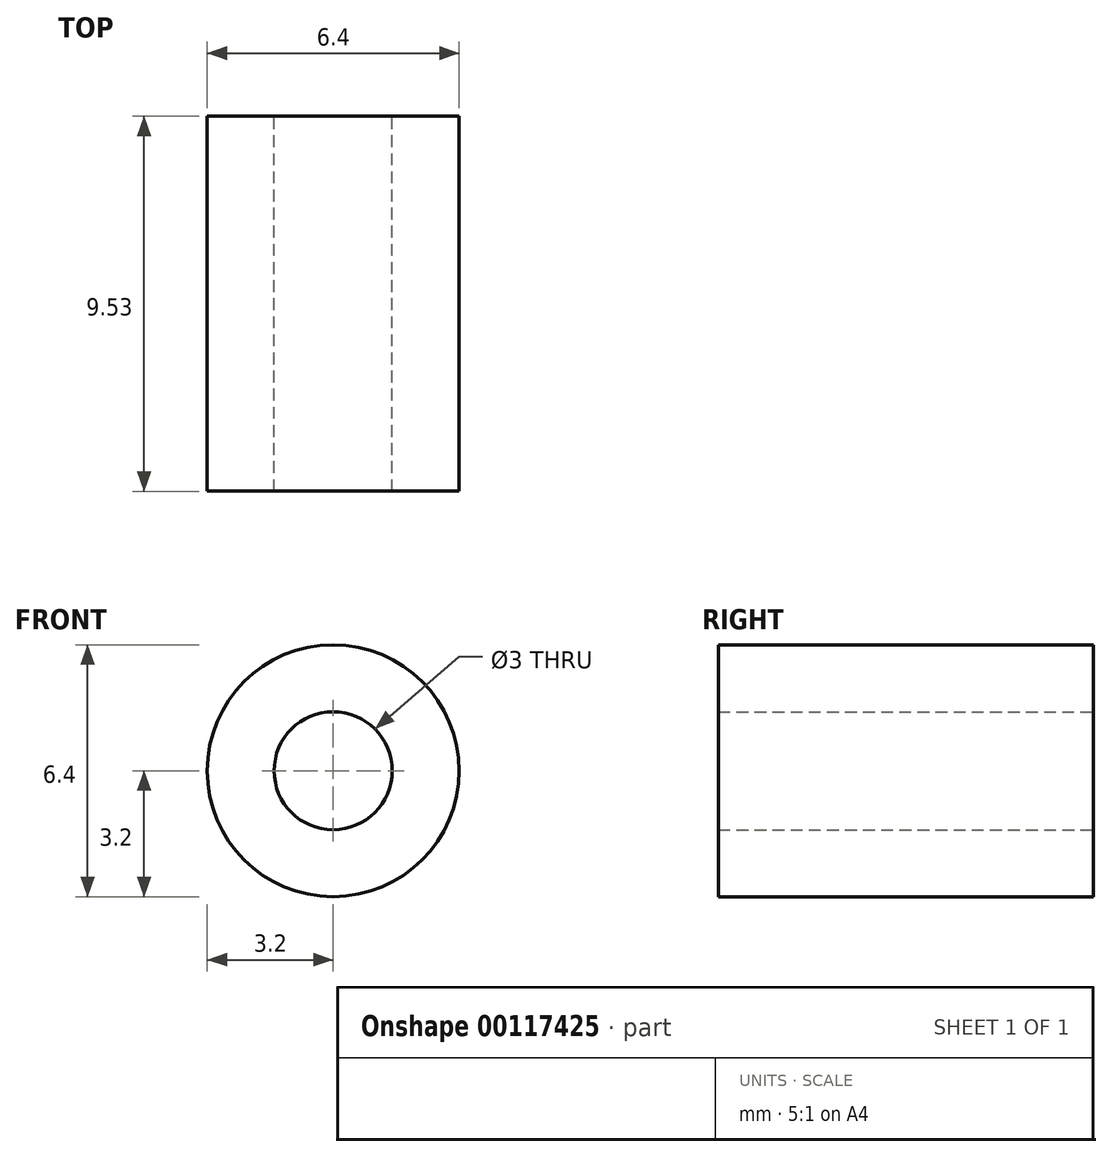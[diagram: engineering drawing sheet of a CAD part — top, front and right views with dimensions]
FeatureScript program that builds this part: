
annotation { "Feature Type Name" : "Feature", "Feature Type Description" : "" }
export const myFeature = defineFeature(function(context is Context, id is Id, definition is map)
    precondition{}
    {
        {
            var Q0;
            Q0=qCreatedBy(makeId("Front.planeOp"),FACE);
            var sketch = newSketch(context, id + "F0", { "sketchPlane" : qUnion([Q0])});
            skCircle(sketch, "E0", {"center": v(0, 0) * mm, "radius": 3.2 * mm});
            skCircle(sketch, "E1", {"center": v(0, 0) * mm, "radius": 1.5 * mm});
            skSolve(sketch);
        }
        {
            var Q0;
            Q0=makeQuery(id+"F0.imprint","IMPRINT",FACE,{"disambiguationData":[TD([[makeQuery(id+"F0.imprint","IMPRINT",EDGE,{"derivedFrom":sQuery(id+"F0.wireOp",EDGE,"E0")}),1.0]])]});
            var Q1;
            Q1=sQuery(id+"F0.wireOp",EDGE,"E1");
            var Q2;
            Q2=sQuery(id+"F0.wireOp",EDGE,"E0");
            extrude(context, id + "F1", {"entities" : qUnion([Q0]), "surfaceEntities" : qUnion([Q1, Q2]), "depth" : 9.52 * mm});
        }
    });
